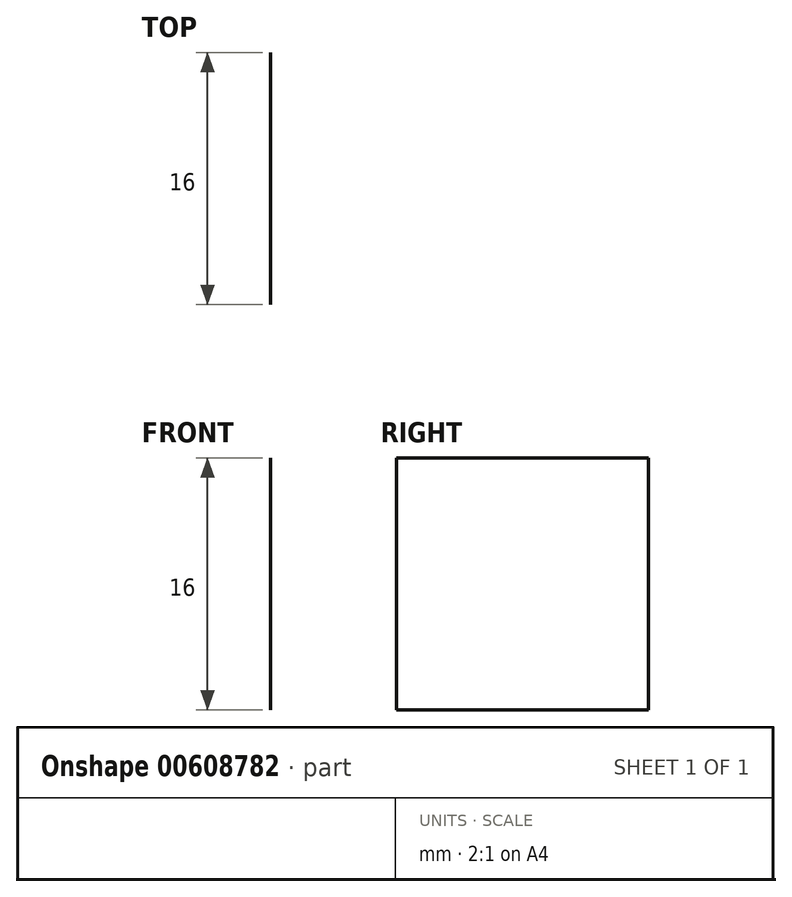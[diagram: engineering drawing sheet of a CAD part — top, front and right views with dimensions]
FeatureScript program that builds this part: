
annotation { "Feature Type Name" : "Feature", "Feature Type Description" : "" }
export const myFeature = defineFeature(function(context is Context, id is Id, definition is map)
    precondition{}
    {
        {
            var Q0;
            Q0=qCreatedBy(makeId("Right.planeOp"),FACE);
            var sketch = newSketch(context, id + "F0", { "sketchPlane" : qUnion([Q0])});
            skLineSegment(sketch, "E0.bottom", {"start": v(0, 0) * mm, "end": v(16, 0) * mm});
            skLineSegment(sketch, "E0.top", {"start": v(0, -16) * mm, "end": v(16, -16) * mm});
            skLineSegment(sketch, "E0.left", {"start": v(0, 0) * mm, "end": v(0, -16) * mm});
            skLineSegment(sketch, "E0.right", {"start": v(16, 0) * mm, "end": v(16, -16) * mm});
            skSolve(sketch);
        }
        {
            var Q0;
            Q0=makeQuery(id+"F0.imprint","IMPRINT",FACE,{"disambiguationData":[TD([[makeQuery(id+"F0.imprint","IMPRINT",EDGE,{"derivedFrom":sQuery(id+"F0.wireOp",EDGE,"E0.bottom")}),-1.0]])]});
            extrude(context, id + "F1", {"entities" : qUnion([Q0]), "depth" : 0 * mm, "offsetDistance" : 25 * mm});
        }
    });
